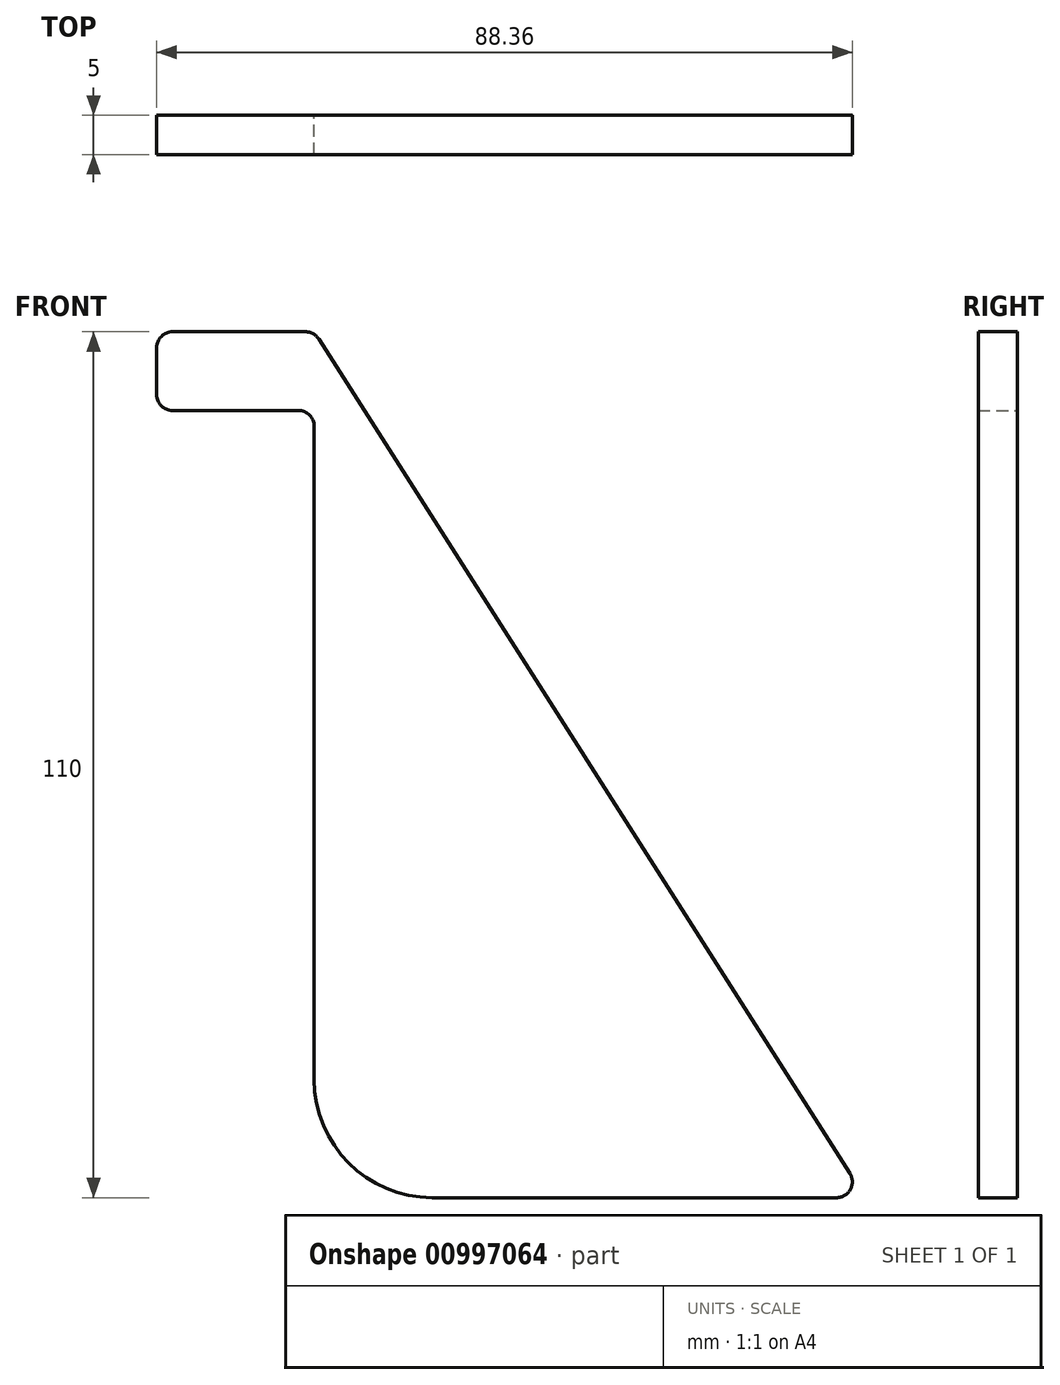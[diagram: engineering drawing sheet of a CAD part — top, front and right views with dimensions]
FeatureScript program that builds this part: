
annotation { "Feature Type Name" : "Feature", "Feature Type Description" : "" }
export const myFeature = defineFeature(function(context is Context, id is Id, definition is map)
    precondition{}
    {
        {
            var Q0;
            Q0=qCreatedBy(makeId("Front.planeOp"),FACE);
            var sketch = newSketch(context, id + "F0", { "sketchPlane" : qUnion([Q0])});
            skLineSegment(sketch, "E0", {"start": v(-18, 100) * mm, "end": v(-2, 100) * mm});
            skLineSegment(sketch, "E1", {"start": v(0, 98) * mm, "end": v(0, 15) * mm});
            skLineSegment(sketch, "E2", {"start": v(15, 0) * mm, "end": v(66.36, 0) * mm});
            skLineSegment(sketch, "E3", {"start": v(0.59, 109.07) * mm, "end": v(68.04, 3.07) * mm});
            skLineSegment(sketch, "E4", {"start": v(-1.1, 110) * mm, "end": v(-18, 110) * mm});
            skLineSegment(sketch, "E5", {"start": v(-20, 108) * mm, "end": v(-20, 102) * mm});
            skPoint(sketch, "E6.visualSharp", {"position": v(0, 0) * mm});
            skArc(sketch, "E6.filletArc", {"start": v(0, 15) * mm, "mid": v(4.4, 4.4) * mm, "end": v(15, 0) * mm});
            skPoint(sketch, "E7.visualSharp", {"position": v(0, 100) * mm});
            skArc(sketch, "E7.filletArc", {"start": v(0, 98) * mm, "mid": v(-0.59, 99.41) * mm, "end": v(-2, 100) * mm});
            skPoint(sketch, "E8.visualSharp", {"position": v(-20, 100) * mm});
            skArc(sketch, "E8.filletArc", {"start": v(-20, 102) * mm, "mid": v(-19.41, 100.59) * mm, "end": v(-18, 100) * mm});
            skPoint(sketch, "E9.visualSharp", {"position": v(-20, 110) * mm});
            skArc(sketch, "E9.filletArc", {"start": v(-18, 110) * mm, "mid": v(-19.41, 109.41) * mm, "end": v(-20, 108) * mm});
            skPoint(sketch, "E10.visualSharp", {"position": v(0, 110) * mm});
            skArc(sketch, "E10.filletArc", {"start": v(0.59, 109.07) * mm, "mid": v(-0.14, 109.75) * mm, "end": v(-1.1, 110) * mm});
            skPoint(sketch, "E11.visualSharp", {"position": v(70, 0) * mm});
            skArc(sketch, "E11.filletArc", {"start": v(66.36, 0) * mm, "mid": v(68.1, 1.04) * mm, "end": v(68.04, 3.07) * mm});
            skSolve(sketch);
        }
        {
            var Q0;
            Q0 = qSketchRegion(id + "F0", true);
            extrude(context, id + "F1", {"entities" : qUnion([Q0]), "depth" : 5 * mm, "offsetDistance" : 25 * mm});
        }
    });
